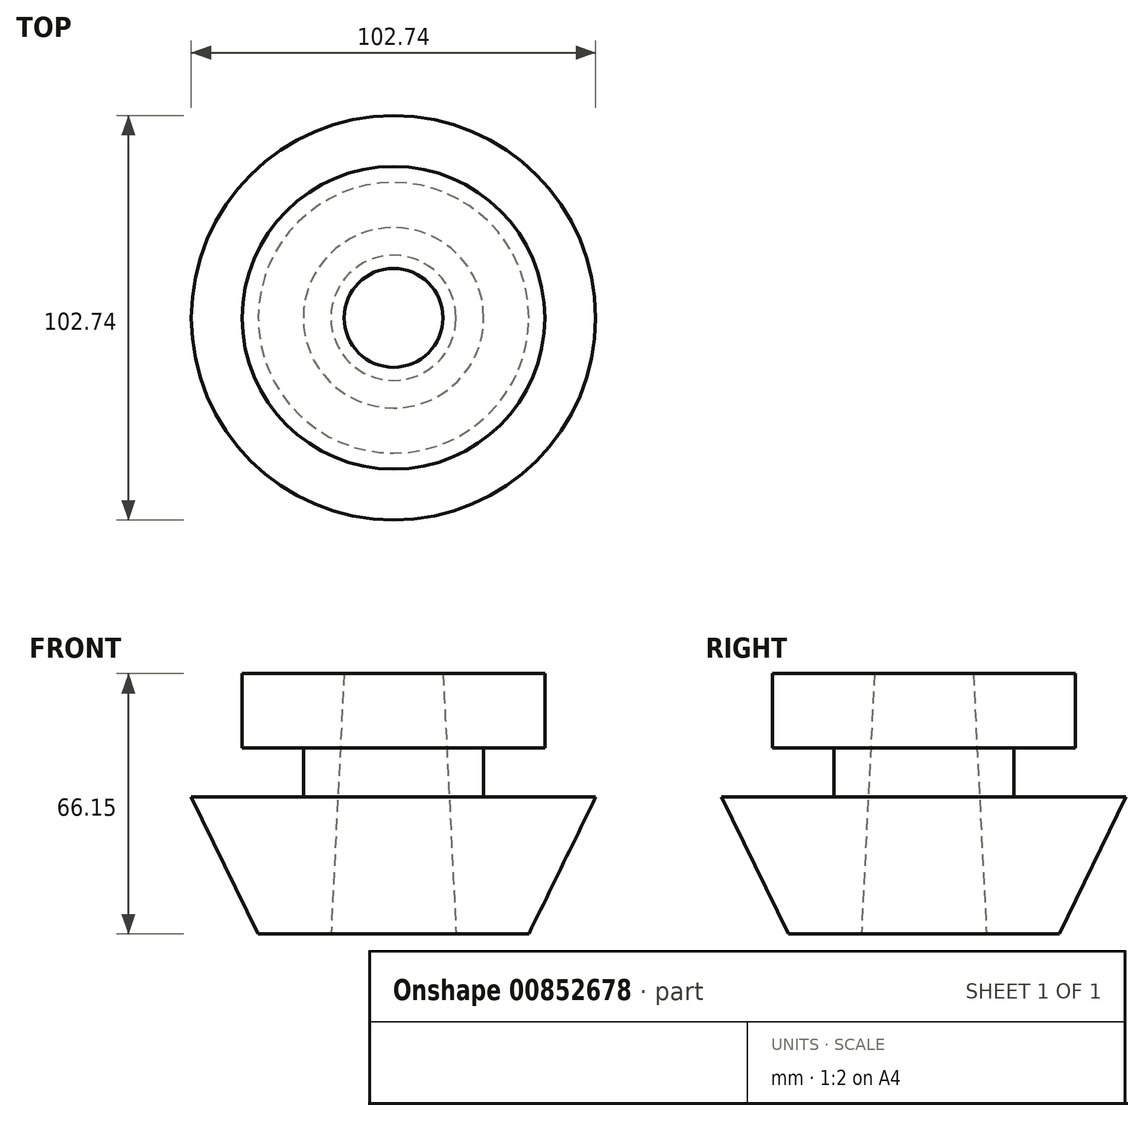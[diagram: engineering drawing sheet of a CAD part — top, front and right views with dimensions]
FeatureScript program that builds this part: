
annotation { "Feature Type Name" : "Feature", "Feature Type Description" : "" }
export const myFeature = defineFeature(function(context is Context, id is Id, definition is map)
    precondition{}
    {
        {
            var Q0;
            Q0=qCreatedBy(makeId("Front.planeOp"),FACE);
            var sketch = newSketch(context, id + "F0", { "sketchPlane" : qUnion([Q0])});
            skLineSegment(sketch, "E0", {"start": v(-15.9, 0) * mm, "end": v(-34.37, 0) * mm});
            skLineSegment(sketch, "E1", {"start": v(-34.37, 0) * mm, "end": v(-51.37, 34.74) * mm});
            skLineSegment(sketch, "E2", {"start": v(-51.37, 34.74) * mm, "end": v(-22.91, 34.74) * mm});
            skLineSegment(sketch, "E3", {"start": v(-22.91, 34.74) * mm, "end": v(-22.91, 47.3) * mm});
            skLineSegment(sketch, "E4", {"start": v(-22.91, 47.3) * mm, "end": v(-38.43, 47.3) * mm});
            skLineSegment(sketch, "E5", {"start": v(-38.43, 47.3) * mm, "end": v(-38.43, 66.15) * mm});
            skLineSegment(sketch, "E6", {"start": v(-38.43, 66.15) * mm, "end": v(-12.56, 66.15) * mm});
            skLineSegment(sketch, "E7", {"start": v(-12.56, 66.15) * mm, "end": v(-15.9, 0) * mm});
            skSolve(sketch);
        }
        {
            var Q0;
            Q0=qCreatedBy(makeId("Front.planeOp"),FACE);
            var sketch = newSketch(context, id + "F1", { "sketchPlane" : qUnion([Q0])});
            skLineSegment(sketch, "E8", {"start": v(0, 126.39) * mm, "end": v(0, -137.47) * mm, "construction": true});
            skSolve(sketch);
        }
        {
            var Q0;
            Q0 = qSketchRegion(id + "F0", true);
            var Q1;
            Q1=sQuery(id+"F1.wireOp",EDGE,"E8");
            revolve(context, id + "F2", {"surfaceOperationType" : NewSurfaceOperationType.NEW, "entities" : qUnion([Q0]), "axis" : qUnion([Q1]), "revolveType" : RevolveType.FULL});
        }
    });
